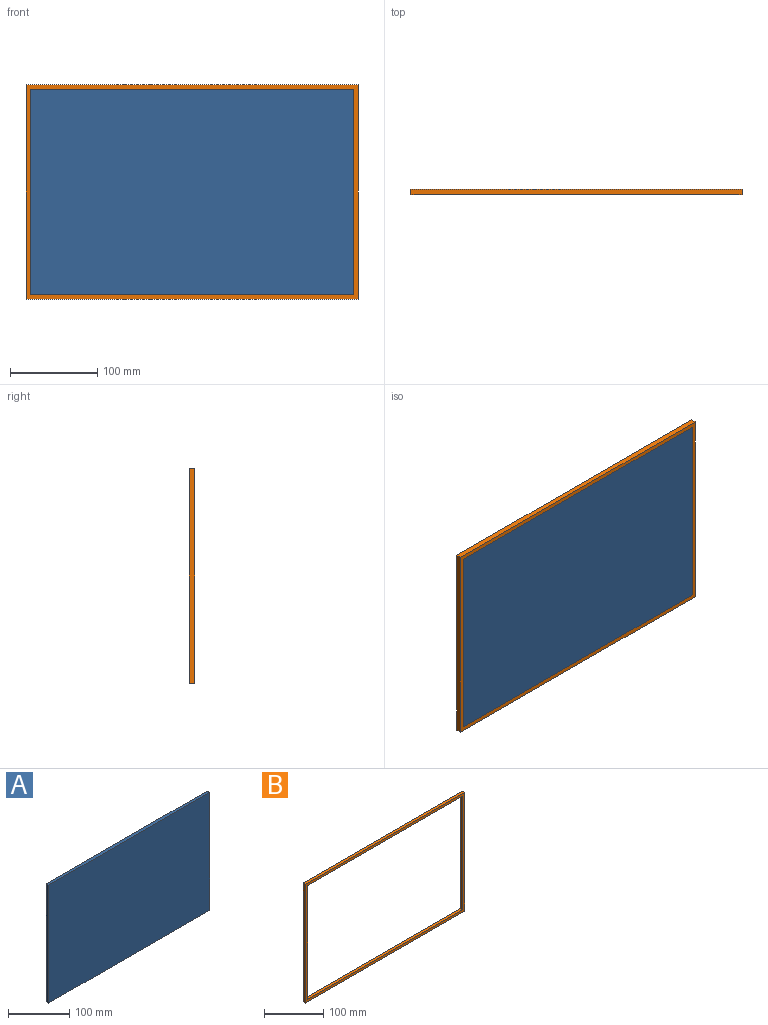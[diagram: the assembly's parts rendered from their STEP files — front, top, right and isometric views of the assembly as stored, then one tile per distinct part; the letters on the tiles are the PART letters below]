
ASSEMBLY  parts=2 mates=1
PART A: 6 faces, bbox 370x5.5x235 mm
  f0: plane 370x5.5mm, normal (0,0,1), area 2035mm2, adj f1,f3,f4,f5
  f1: plane 235x5.5mm, normal (-1,0,0), area 1292.5mm2, adj f0,f2,f4,f5
  f2: plane 370x5.5mm, normal (0,0,-1), area 2035mm2, adj f1,f3,f4,f5
  f3: plane 235x5.5mm, normal (1,0,0), area 1292.5mm2, adj f0,f2,f4,f5
  f4: plane 370x235mm, normal (0,-1,0), area 86950mm2, adj f0,f1,f2,f3
  f5: plane 370x235mm, normal (0,1,0), area 86950mm2, adj f0,f1,f2,f3
PART B: 10 faces, bbox 380x6x245 mm
  f0: plane 380x6mm, normal (0,0,1), area 2280mm2, adj f1,f7,f8,f9
  f1: plane 245x6mm, normal (-1,0,0), area 1470mm2, adj f0,f2,f8,f9
  f2: plane 380x6mm, normal (0,0,-1), area 2280mm2, adj f1,f7,f8,f9
  f3: plane 235x6mm, normal (1,0,0), area 1410mm2, adj f4,f6,f8,f9
  f4: plane 370x6mm, normal (0,0,-1), area 2220mm2, adj f3,f5,f8,f9
  f5: plane 235x6mm, normal (-1,0,0), area 1410mm2, adj f4,f6,f8,f9
  f6: plane 370x6mm, normal (0,0,1), area 2220mm2, adj f3,f5,f8,f9
  f7: plane 245x6mm, normal (1,0,0), area 1470mm2, adj f0,f2,f8,f9
  f8: plane 380x245mm, normal (0,-1,0), area 6150mm2, adj f0,f1,f2,f3,f4,f5,f6,f7
  f9: plane 380x245mm, normal (0,1,0), area 6150mm2, adj f0,f1,f2,f3,f4,f5,f6,f7
PLACE A t=(0,5.5,0)mm
PLACE B t=(0,6,0)mm
MATE fastened B.f6 <-> A.f2  axis (0,0,1) through (-185,0,-117.5)mm
